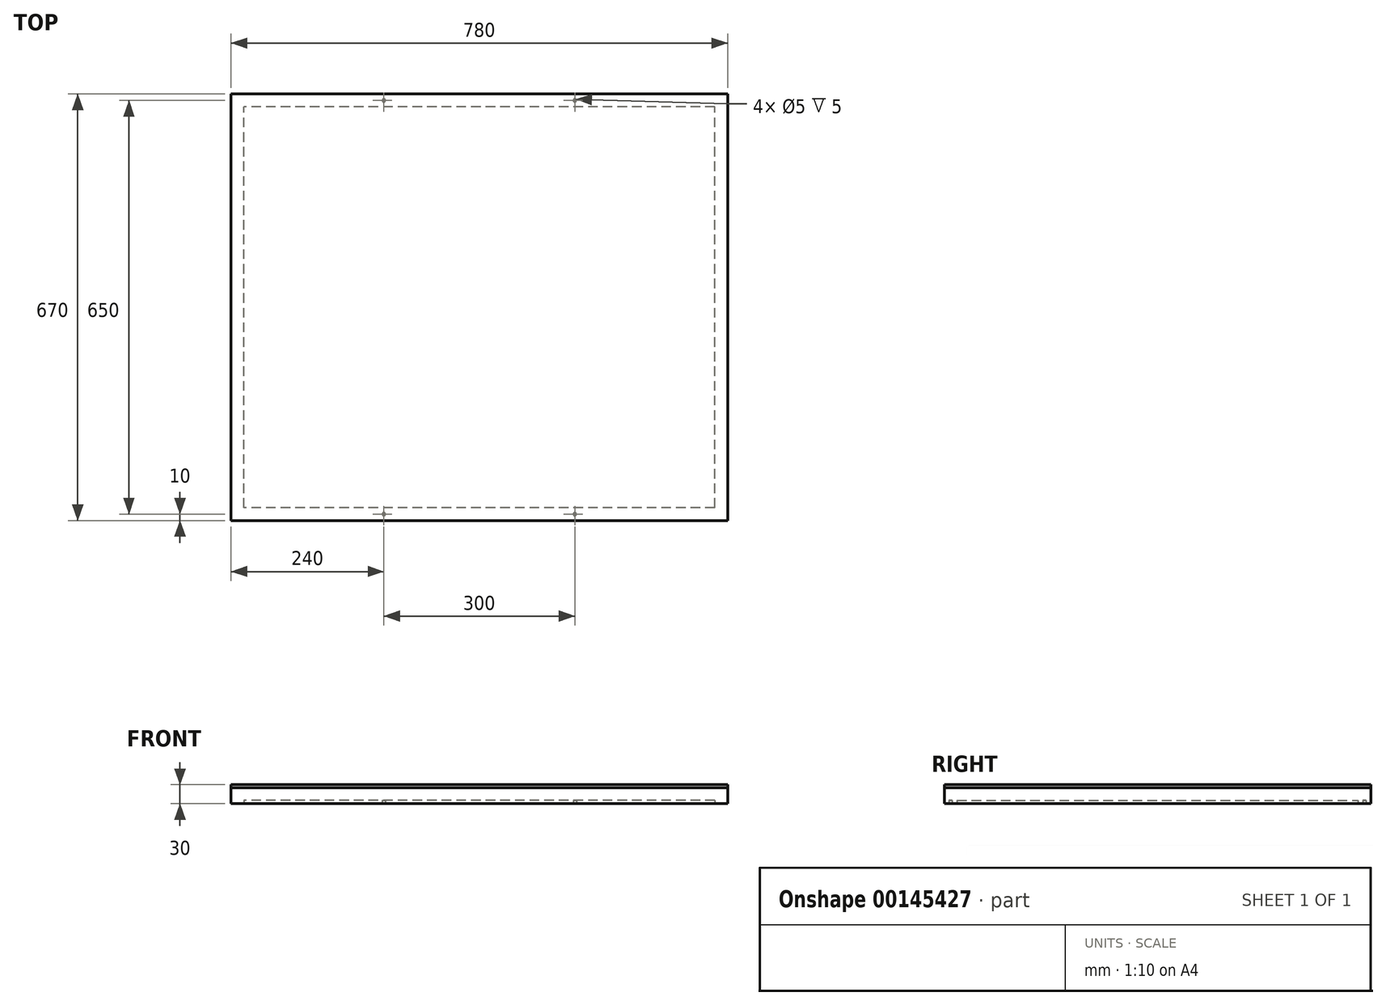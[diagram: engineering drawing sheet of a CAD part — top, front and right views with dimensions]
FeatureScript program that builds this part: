
annotation { "Feature Type Name" : "Feature", "Feature Type Description" : "" }
export const myFeature = defineFeature(function(context is Context, id is Id, definition is map)
    precondition{}
    {
        {
            var Q0;
            Q0=qCreatedBy(makeId("Top.planeOp"),FACE);
            var sketch = newSketch(context, id + "F0", { "sketchPlane" : qUnion([Q0])});
            skLineSegment(sketch, "E0.bottom", {"start": v(390, -335) * mm, "end": v(-390, -335) * mm});
            skLineSegment(sketch, "E0.top", {"start": v(390, 335) * mm, "end": v(-390, 335) * mm});
            skLineSegment(sketch, "E0.left", {"start": v(390, -335) * mm, "end": v(390, 335) * mm});
            skLineSegment(sketch, "E0.right", {"start": v(-390, -335) * mm, "end": v(-390, 335) * mm});
            skPoint(sketch, "E0.middle", {"position": v(0, 0) * mm});
            skSolve(sketch);
        }
        {
            var Q0;
            Q0=qSketchRegion(id+"F0",true);
            extrude(context, id + "F1", {"entities" : qUnion([Q0]), "depth" : 25 * mm});
        }
        {
            var Q0;
            Q0=makeQuery(id+"F1.opExtrude","CAP_FACE",FACE,{"disambiguationData":[OSD([sQuery(id+"F0.wireOp",EDGE,"E0.bottom"),sQuery(id+"F0.wireOp",EDGE,"E0.top"),sQuery(id+"F0.wireOp",EDGE,"E0.left"),sQuery(id+"F0.wireOp",EDGE,"E0.right")])],"isStart":true});
            shell(context, id + "F2", {"entities" : qUnion([Q0]), "thickness" : 20 * mm});
        }
        {
            var Q0;
            Q0=makeQuery(id+"F1.opExtrude","CAP_FACE",FACE,{"disambiguationData":[OSD([sQuery(id+"F0.wireOp",EDGE,"E0.bottom"),sQuery(id+"F0.wireOp",EDGE,"E0.top"),sQuery(id+"F0.wireOp",EDGE,"E0.left"),sQuery(id+"F0.wireOp",EDGE,"E0.right")])],"isStart":true});
            var sketch = newSketch(context, id + "F3", { "sketchPlane" : qUnion([Q0])});
            skPoint(sketch, "E1.centerSnap0", {"position": v(0, 315) * mm});
            skCircle(sketch, "E2", {"center": v(-150, 325) * mm, "radius": 2.5 * mm});
            skLineSegment(sketch, "E3.0", {"start": v(390, 335) * mm, "end": v(-390, 335) * mm});
            skLineSegment(sketch, "E3.1", {"start": v(370, 315) * mm, "end": v(-370, 315) * mm});
            skCircle(sketch, "E4.MirrorC", {"center": v(150, 325) * mm, "radius": 2.5 * mm});
            skCircle(sketch, "E5.MirrorC", {"center": v(150, -325) * mm, "radius": 2.5 * mm});
            skCircle(sketch, "E6.MirrorC", {"center": v(-150, -325) * mm, "radius": 2.5 * mm});
            skSolve(sketch);
        }
        {
            var Q0;
            Q0=qSketchRegion(id+"F3",true);
            extrude(context, id + "F4", {"entities" : qUnion([Q0]), "operationType" : NewBodyOperationType.REMOVE, "oppositeDirection" : true, "depth" : 5 * mm});
        }
        {
            var Q0;
            Q0=makeQuery(id+"F1.opExtrude","CAP_FACE",FACE,{"disambiguationData":[OSD([sQuery(id+"F0.wireOp",EDGE,"E0.bottom"),sQuery(id+"F0.wireOp",EDGE,"E0.top"),sQuery(id+"F0.wireOp",EDGE,"E0.left"),sQuery(id+"F0.wireOp",EDGE,"E0.right")])],"isStart":false});
            var sketch = newSketch(context, id + "F5", { "sketchPlane" : qUnion([Q0])});
            skLineSegment(sketch, "E7.0", {"start": v(390, 335) * mm, "end": v(-390, 335) * mm});
            skLineSegment(sketch, "E8.0", {"start": v(-390, -335) * mm, "end": v(-390, 335) * mm});
            skLineSegment(sketch, "E9.0", {"start": v(390, -335) * mm, "end": v(390, 335) * mm});
            skLineSegment(sketch, "E10.0", {"start": v(390, -335) * mm, "end": v(-390, -335) * mm});
            skSolve(sketch);
        }
        {
            var Q0;
            Q0=qSketchRegion(id+"F5",true);
            extrude(context, id + "F6", {"entities" : qUnion([Q0]), "depth" : 5 * mm});
        }
    });
